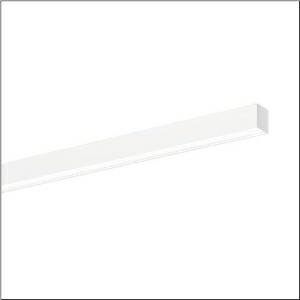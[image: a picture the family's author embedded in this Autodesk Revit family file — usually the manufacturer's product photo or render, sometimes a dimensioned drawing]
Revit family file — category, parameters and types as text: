
# Revit family: silica_r__21_51mx20da42wb_78eb
name_source: partatom
category: Lighting Fixtures
units: mm (PartAtom-declared; Revit-internal decimal feet)

## family parameters
Cut with Voids When Loaded = No
Host = Face
Light Source = No
Part Type = Normal
Room Calculation Point = No
Round Connector Dimension = Use Diameter
Shared = No

## types (1)
- --- (1 x LED, 2400 lm, 15.2 W, 4000K)
    Apparent Load = 15 VA
    CIE Flux Codes = 48 79 96 100 100
    Color Rendering = 80
    Color Temperature = 4000K
    Default Elevation = 1800 mm
    Description = Silica® 21, office luminaire, primary optical cover: cover, of PMMA, opal, light emission: direct distribution, primary light characteristic: symmetric, installation type: surface-mounted, LED, rated luminous flux: 2.400lm, luminous efficacy: 158lm/W, light colour: 840, colour temperature: 4000K, control gear: DALI 2, with terminal, 3+2-pole, max. 2.5mm², mains connection: 220..240V, AC, 50/60Hz, rated input power: 15.2W, luminaire housing, of aluminium, traffic white (RAL 9016), length: 1.204mm, width: 53mm, height: 53mm, protection rating (complete): IP20, insulation class (complete): insulation class I (protective earthing), certification: CE, permissible operating ambient temperature: 0..+35°C, standard: EN 50419, packaging unit: 1 piece
    Height = 53 mm
    Lamp = 1 x LED
    Lamp Light Flux = 2400 lm
    Lamp Power = 15.2 W
    Lamp count = 1
    Length = 1204 mm
    Luminous efficacy = 158 lm/W
    Manufacturer = Siteco
    ModVariant = No
    Model = 51MX20DA42WB
    Mounting Place = Ceiling
    Mounting Type = Surface mounted
    Number of Poles = 1
    OnlyDefault = Yes
    Power Factor = 1
    Product Name = Silica® 21
    Product group = office luminaire | ceiling mounted
    ProductGroupID = 303
    Protection Class = Protection class I
    Protection Degree = IP 20
    RLX_Detail_Level = 1
    RLX_Emergency_Light_Flux = 0 lm
    RLX_Emergency_Type = 0
    RLX_Emergency_Type_DB = No
    RlxData = <blob elided: 23797 chars, md5=4d953c11>
    Socket = socket
    Standby Power = 0 W
    System Light Flux = 2400 lm
    System Power = 15 W
    Type Comments = factory setting: luminous flux: 100 % | dim-lin: 254 | 218 mA
    Type Image = l_1335877.jpg
    URL = http://relux.com
    VarID = @adj_026827
    Voltage = 0 V
    Weight = 0.00 kg
    Width = 53 mm

## geometry (parser evidence)
native form markers: Blend x4, Sweep x11
no freeform markers — native parametric forms only
